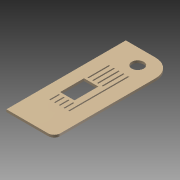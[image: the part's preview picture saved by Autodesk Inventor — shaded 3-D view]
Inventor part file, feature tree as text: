
AUTODESK INVENTOR PART (.ipt)
format: ipt  version: 2015 (Build 190159000, 159)  size: 198,656 bytes
history: native  units: mm
features: sketch x6, extrude x5, other x1, hole x1
ambient origin geometry x8: Origin, YZ Plane, XZ Plane, XY Plane, X Axis, Y Axis, Z Axis, Center Point
bodies: Body1 (feature_tree)
feature tree (13):
  other  "Sólido1"
  extrude  "Extrusión1"  Depth=10.0mm
  extrude  "Extrusión2"  Depth=40.0mm
  hole  "Agujero1"  [1 undecoded]
  extrude  "Extrusión3"  Depth=5.0mm
  extrude  "Extrusión4"  Depth=2.5mm
  extrude  "Extrusión5"  Depth=10.0mm
  sketch  "Boceto1"  dims[d3=30.0mm d4=10.0mm]
  sketch  "Boceto2"  dims[d5=100.0mm d6=40.0mm]
  sketch  "Boceto3"  dims[d7=2.0mm d8=0.0mm d9=2.5mm]
  sketch  "Boceto4"  dims[d10=5.0mm d11=5.0mm]
  sketch  "Boceto5"  dims[d12=2.5mm d13=2.5mm]
  sketch  "Boceto6"  dims[d14=2.5mm d15=2.5mm d16=2.5mm d17=10.0mm d18=20.0mm d19=20.0mm d20=20.0mm d21=2.5mm d22=20.0mm d23=2.0mm d24=2.0mm d25=2.0mm d26=2.0mm d27=2.0mm d28=2.0mm d29=2.0mm d30=5.0mm d31=0.0mm d32=23.0mm d33=13.0mm d34=10.0mm d35=6.0mm d36=4.0mm d37=2.0mm d38=90.0deg d39=8.0mm d40=20.594885mm d41=1.0mm d42=50.0mm d43=1.0mm d44=50.0mm d45=1.0mm d46=50.0mm d47=1.0mm d48=50.0mm d49=1.0mm d50=50.0mm d51=3.0mm d52=3.0mm d53=3.0mm d54=3.0mm d55=10.0mm d56=0.0mm d57=45.0mm d58=65.0mm d59=30.0mm d60=22.0mm d61=10.0mm d62=20.0mm d63=45.0mm d64=12.0mm d65=10.0mm d66=0.0mm d67=2.0mm d68=10.0mm d69=0.0mm]
note: 1 required parameter value undecoded (feature->parameter linkage not recoverable at this tier; creation-order binding heuristic only, values carry confidence <= 0.55)
